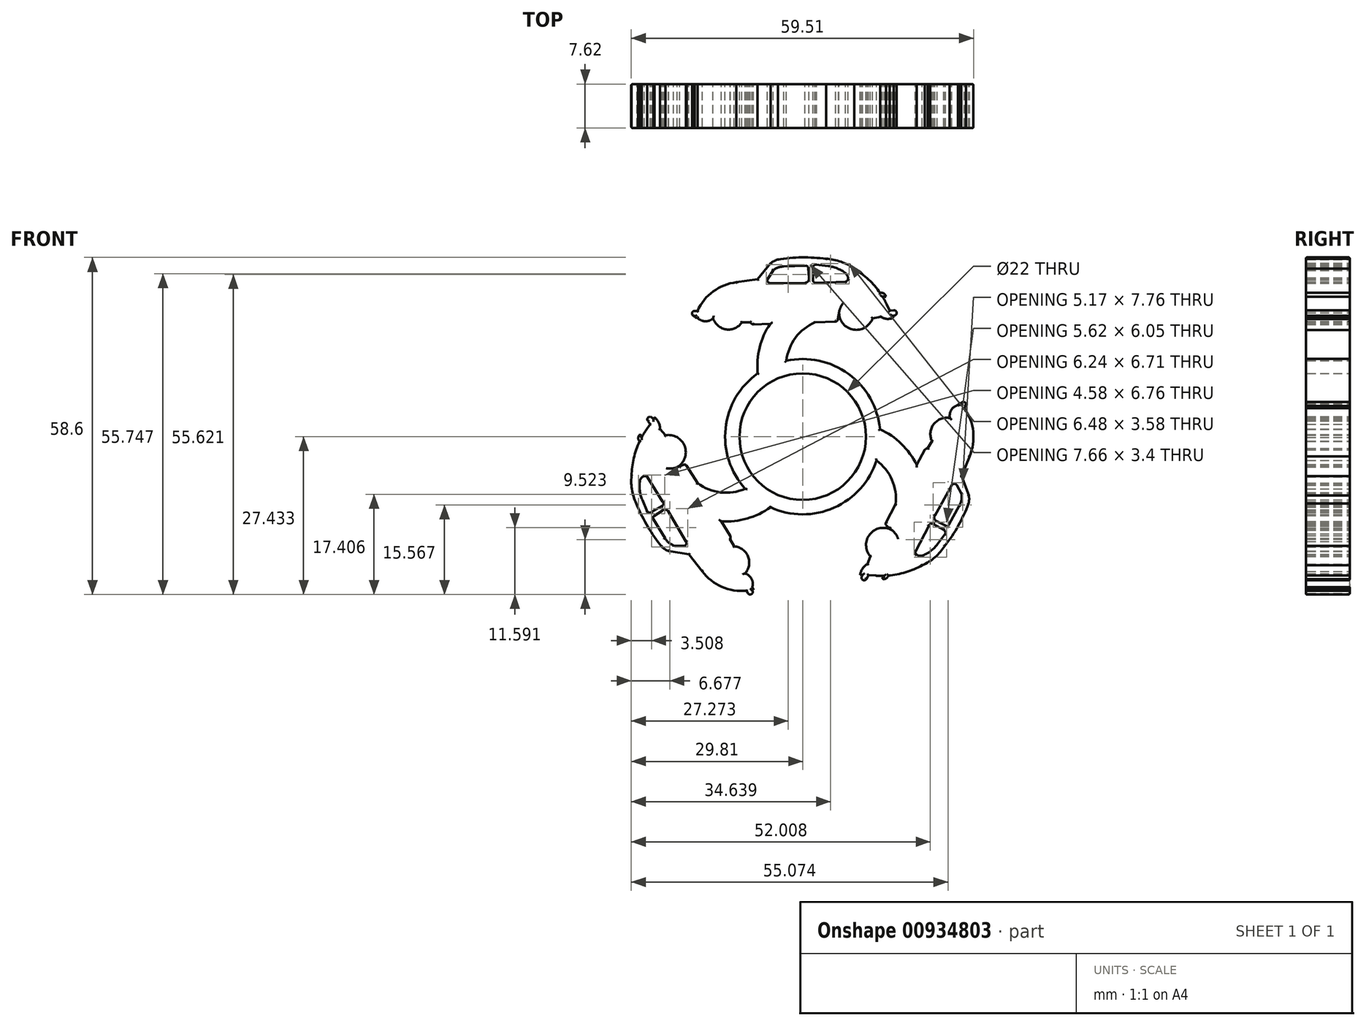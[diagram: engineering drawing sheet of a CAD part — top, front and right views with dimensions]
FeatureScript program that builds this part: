
annotation { "Feature Type Name" : "Feature", "Feature Type Description" : "" }
export const myFeature = defineFeature(function(context is Context, id is Id, definition is map)
    precondition{}
    {
        {
            var Q0;
            Q0=qCreatedBy(makeId("Front.planeOp"),FACE);
            var sketch = newSketch(context, id + "F0", { "sketchPlane" : qUnion([Q0])});
            skArc(sketch, "E0", {"start": v(-11.53, 23.27) * mm, "mid": v(-15.57, 21.68) * mm, "end": v(-18.3, 18.3) * mm});
            skArc(sketch, "E1", {"start": v(8.99, 25.61) * mm, "mid": v(6.65, 26.83) * mm, "end": v(4.07, 27.35) * mm});
            skArc(sketch, "E2", {"start": v(-15.59, 17) * mm, "mid": v(-13.3, 15.08) * mm, "end": v(-10.57, 16.27) * mm});
            skArc(sketch, "E3", {"start": v(6.32, 17.98) * mm, "mid": v(8.82, 15.04) * mm, "end": v(12.15, 17) * mm});
            skPoint(sketch, "E4.first.point", {"position": v(-9.3, 16.64) * mm});
            skPoint(sketch, "E4.second.point", {"position": v(-16.14, 17.08) * mm});
            skPoint(sketch, "E4.third.point", {"position": v(-15.9, 15.72) * mm});
            skPoint(sketch, "E5.first.point", {"position": v(6.84, 18.84) * mm});
            skPoint(sketch, "E5.second.point", {"position": v(12.55, 16.03) * mm});
            skPoint(sketch, "E5.third.point", {"position": v(9.32, 20.48) * mm});
            skLineSegment(sketch, "E6", {"start": v(-7.85, 23.8) * mm, "end": v(-5.6, 26.57) * mm});
            skLineSegment(sketch, "E7", {"start": v(-7.85, 23.8) * mm, "end": v(-11.53, 23.27) * mm});
            skPoint(sketch, "E8.second.point", {"position": v(-0.88, 20.92) * mm});
            skPoint(sketch, "E8.third.point", {"position": v(0.26, 22.68) * mm});
            skPoint(sketch, "E9.first.point", {"position": v(12.94, 17.76) * mm});
            skPoint(sketch, "E9.second.point", {"position": v(14.7, 18.65) * mm});
            skPoint(sketch, "E9.third.point", {"position": v(14.48, 18.97) * mm});
            skPoint(sketch, "E10.first.point", {"position": v(12.5, 18.64) * mm});
            skPoint(sketch, "E10.second.point", {"position": v(16.16, 21.44) * mm});
            skPoint(sketch, "E10.third.point", {"position": v(16.02, 21.52) * mm});
            skPoint(sketch, "E11.first.point", {"position": v(11.44, 23.75) * mm});
            skArc(sketch, "E12", {"start": v(-18.74, 17.14) * mm, "mid": v(-18.5, 17.1) * mm, "end": v(-18.27, 17.1) * mm});
            skPoint(sketch, "E12.first.point", {"position": v(-15.9, 18.25) * mm});
            skPoint(sketch, "E12.second.point", {"position": v(-20.76, 21.48) * mm});
            skPoint(sketch, "E12.third.point", {"position": v(-20.1, 17.77) * mm});
            skArc(sketch, "E13", {"start": v(-9.13, 16.27) * mm, "mid": v(-8.75, 16) * mm, "end": v(-8.27, 15.97) * mm});
            skPoint(sketch, "E13.second.point", {"position": v(-7.64, 17.02) * mm});
            skPoint(sketch, "E13.third.point", {"position": v(-8.6, 15.96) * mm});
            skLineSegment(sketch, "E14.trimOffspring", {"start": v(-8.6, 15.96) * mm, "end": v(-8.27, 15.97) * mm});
            skArc(sketch, "E15.trimOffspring", {"start": v(-4.34, 27.23) * mm, "mid": v(-5, 26.96) * mm, "end": v(-5.6, 26.57) * mm});
            skArc(sketch, "E16.trimOffspring", {"start": v(16.16, 21.44) * mm, "mid": v(16.09, 21.48) * mm, "end": v(16.02, 21.52) * mm});
            skArc(sketch, "E17.trimOffspring", {"start": v(14.61, 19.44) * mm, "mid": v(14.26, 20.12) * mm, "end": v(13.88, 20.77) * mm});
            skPoint(sketch, "E18.first.point", {"position": v(-9.43, 17.2) * mm});
            skPoint(sketch, "E18.second.point", {"position": v(-16.83, 16.34) * mm});
            skPoint(sketch, "E18.third.point", {"position": v(-14.78, 13.44) * mm});
            skArc(sketch, "E19", {"start": v(4.07, 27.35) * mm, "mid": v(-0.14, 27.6) * mm, "end": v(-4.34, 27.23) * mm});
            skPoint(sketch, "E20.end.orphan", {"position": v(4.07, 27.35) * mm});
            skArc(sketch, "E21", {"start": v(14.46, 20.77) * mm, "mid": v(14.1, 21.32) * mm, "end": v(13.47, 21.4) * mm});
            skPoint(sketch, "E21.first.point", {"position": v(13.47, 21.4) * mm});
            skPoint(sketch, "E21.second.point", {"position": v(13.78, 19.9) * mm});
            skPoint(sketch, "E21.third.point", {"position": v(14.26, 20.13) * mm});
            skLineSegment(sketch, "E22", {"start": v(14.46, 20.77) * mm, "end": v(13.88, 20.77) * mm});
            skArc(sketch, "E23.trimOffspring", {"start": v(13.47, 21.4) * mm, "mid": v(11.45, 23.74) * mm, "end": v(8.99, 25.61) * mm});
            skLineSegment(sketch, "E24", {"start": v(14.61, 19.44) * mm, "end": v(15.14, 18.36) * mm});
            skArc(sketch, "E25", {"start": v(15.9, 17.47) * mm, "mid": v(16.34, 17.97) * mm, "end": v(15.83, 18.4) * mm});
            skLineSegment(sketch, "E26", {"start": v(15.9, 17.47) * mm, "end": v(15.59, 17.45) * mm});
            skLineSegment(sketch, "E27", {"start": v(15.83, 18.4) * mm, "end": v(15.14, 18.36) * mm});
            skPoint(sketch, "E27.endSnap0", {"position": v(15.2, 18.26) * mm});
            skPoint(sketch, "E28.orphan", {"position": v(15.2, 18.36) * mm});
            skArc(sketch, "E29", {"start": v(-18.76, 18.3) * mm, "mid": v(-19.25, 17.87) * mm, "end": v(-18.83, 17.37) * mm});
            skArc(sketch, "E30.trimOffspring", {"start": v(-18.67, 17.37) * mm, "mid": v(-18.7, 17.25) * mm, "end": v(-18.74, 17.14) * mm});
            skLineSegment(sketch, "E31", {"start": v(-18.8, 18.3) * mm, "end": v(-18.3, 18.3) * mm});
            skLineSegment(sketch, "E32", {"start": v(-18.83, 17.37) * mm, "end": v(-18.67, 17.37) * mm});
            skPoint(sketch, "E33.orphan", {"position": v(-18.3, 17.38) * mm});
            skPoint(sketch, "E34.orphan", {"position": v(-18.66, 17.38) * mm});
            skLineSegment(sketch, "E35.trimOffspring", {"start": v(15.59, 17.45) * mm, "end": v(15.77, 17.08) * mm});
            skPoint(sketch, "E36.first.point", {"position": v(7.3, 19.61) * mm});
            skPoint(sketch, "E36.second.point", {"position": v(11.9, 14.6) * mm});
            skPoint(sketch, "E36.third.point", {"position": v(12.82, 16.03) * mm});
            skArc(sketch, "E37", {"start": v(5.67, 16.42) * mm, "mid": v(5.96, 16.53) * mm, "end": v(6.12, 16.8) * mm});
            skPoint(sketch, "E37.first.point", {"position": v(6.12, 16.93) * mm});
            skPoint(sketch, "E37.second.point", {"position": v(5.22, 16.82) * mm});
            skPoint(sketch, "E37.third.point", {"position": v(5.67, 16.42) * mm});
            skLineSegment(sketch, "E38", {"start": v(6.23, 17.51) * mm, "end": v(6.12, 16.8) * mm});
            skArc(sketch, "E39.trimOffspring", {"start": v(6.32, 17.98) * mm, "mid": v(6.27, 17.75) * mm, "end": v(6.23, 17.51) * mm});
            skPoint(sketch, "E40.first.point", {"position": v(0.33, 26.04) * mm});
            skPoint(sketch, "E40.second.point", {"position": v(0.73, 25.33) * mm});
            skPoint(sketch, "E40.third.point", {"position": v(0.53, 25.3) * mm});
            skArc(sketch, "E41", {"start": v(0.4, 23.19) * mm, "mid": v(0.94, 23.44) * mm, "end": v(1.07, 24.03) * mm});
            skPoint(sketch, "E41.first.point", {"position": v(1.07, 23.71) * mm});
            skPoint(sketch, "E41.second.point", {"position": v(-0.24, 24.08) * mm});
            skPoint(sketch, "E41.third.point", {"position": v(0.4, 23.19) * mm});
            skArc(sketch, "E42", {"start": v(-6.05, 23.94) * mm, "mid": v(-6.11, 23.4) * mm, "end": v(-5.64, 23.12) * mm});
            skPoint(sketch, "E42.first.point", {"position": v(-5.92, 23.19) * mm});
            skPoint(sketch, "E42.second.point", {"position": v(-5.35, 24) * mm});
            skPoint(sketch, "E42.third.point", {"position": v(-5.6, 24.12) * mm});
            skArc(sketch, "E43", {"start": v(-3.31, 26.01) * mm, "mid": v(-4.29, 25.83) * mm, "end": v(-5.15, 25.33) * mm});
            skPoint(sketch, "E43.first.point", {"position": v(-5.15, 25.33) * mm});
            skPoint(sketch, "E43.second.point", {"position": v(-1.4, 21) * mm});
            skPoint(sketch, "E43.third.point", {"position": v(-0.47, 23.64) * mm});
            skLineSegment(sketch, "E44", {"start": v(-5.15, 25.33) * mm, "end": v(-6.08, 23.9) * mm});
            skLineSegment(sketch, "E45", {"start": v(-3.31, 26.01) * mm, "end": v(0.56, 26.12) * mm});
            skLineSegment(sketch, "E46", {"start": v(-5.64, 23.12) * mm, "end": v(0.4, 23.19) * mm});
            skLineSegment(sketch, "E47", {"start": v(1.07, 24.03) * mm, "end": v(0.98, 25.73) * mm});
            skArc(sketch, "E48.trimOffspring", {"start": v(0.98, 25.73) * mm, "mid": v(0.75, 26.08) * mm, "end": v(0.33, 26.04) * mm});
            skArc(sketch, "E49.trimOffspring", {"start": v(-6.05, 23.95) * mm, "mid": v(-6.05, 23.95) * mm, "end": v(-6.05, 23.94) * mm});
            skArc(sketch, "E50", {"start": v(2.25, 26.33) * mm, "mid": v(1.9, 26.13) * mm, "end": v(1.79, 25.75) * mm});
            skPoint(sketch, "E50.first.point", {"position": v(1.79, 25.85) * mm});
            skPoint(sketch, "E50.second.point", {"position": v(2.85, 25.68) * mm});
            skPoint(sketch, "E50.third.point", {"position": v(2.05, 25.34) * mm});
            skArc(sketch, "E51", {"start": v(1.8, 23.68) * mm, "mid": v(1.96, 23.26) * mm, "end": v(2.41, 23.19) * mm});
            skPoint(sketch, "E51.first.point", {"position": v(1.8, 23.68) * mm});
            skPoint(sketch, "E51.second.point", {"position": v(2.7, 23.57) * mm});
            skPoint(sketch, "E51.third.point", {"position": v(2.7, 23.72) * mm});
            skPoint(sketch, "E52.first.point", {"position": v(7.78, 23.5) * mm});
            skPoint(sketch, "E52.second.point", {"position": v(5.63, 24.43) * mm});
            skPoint(sketch, "E52.third.point", {"position": v(5.78, 23.24) * mm});
            skArc(sketch, "E53", {"start": v(1.79, 25.8) * mm, "mid": v(1.79, 25.8) * mm, "end": v(1.79, 25.8) * mm});
            skPoint(sketch, "E53.first.point", {"position": v(7.41, 24.88) * mm});
            skPoint(sketch, "E53.second.point", {"position": v(-0.05, 15.42) * mm});
            skPoint(sketch, "E53.third.point", {"position": v(3.06, 26.08) * mm});
            skArc(sketch, "E54", {"start": v(7.46, 23.38) * mm, "mid": v(7.7, 23.51) * mm, "end": v(7.85, 23.74) * mm});
            skPoint(sketch, "E54.first.point", {"position": v(7.46, 23.38) * mm});
            skPoint(sketch, "E54.second.point", {"position": v(7.16, 24.47) * mm});
            skPoint(sketch, "E54.third.point", {"position": v(7.12, 24.46) * mm});
            skLineSegment(sketch, "E55", {"start": v(2.41, 23.19) * mm, "end": v(7.46, 23.38) * mm});
            skLineSegment(sketch, "E56", {"start": v(2.25, 26.33) * mm, "end": v(4.45, 26.08) * mm});
            skLineSegment(sketch, "E57", {"start": v(1.79, 25.85) * mm, "end": v(1.8, 23.68) * mm});
            skArc(sketch, "E58.trimOffspring", {"start": v(7.85, 23.74) * mm, "mid": v(7.8, 24.38) * mm, "end": v(7.41, 24.88) * mm});
            skArc(sketch, "E59.trimOffspring", {"start": v(7.41, 24.88) * mm, "mid": v(6, 25.68) * mm, "end": v(4.45, 26.08) * mm});
            skPoint(sketch, "E60.first.point", {"position": v(-17.23, 16.52) * mm});
            skPoint(sketch, "E60.second.point", {"position": v(-16.33, 20.19) * mm});
            skPoint(sketch, "E60.third.point", {"position": v(-16.6, 20.25) * mm});
            skArc(sketch, "E61.trimOffspring", {"start": v(-18.27, 17.1) * mm, "mid": v(-16.95, 16.5) * mm, "end": v(-15.59, 17) * mm});
            skLineSegment(sketch, "E62", {"start": v(-10.57, 16.27) * mm, "end": v(-9.13, 16.27) * mm});
            skLineSegment(sketch, "E63", {"start": v(12.15, 17) * mm, "end": v(13.57, 17.26) * mm});
            skArc(sketch, "E64.trimOffspring", {"start": v(13.57, 17.26) * mm, "mid": v(14.65, 16.9) * mm, "end": v(15.77, 17.08) * mm});
            skPoint(sketch, "E65.1.36", {"position": v(-25.13, -61.05) * mm});
            skPoint(sketch, "E66", {"position": v(-1.45, 16.2) * mm});
            skLineSegment(sketch, "E67", {"start": v(-8.6, 15.96) * mm, "end": v(-5.67, 16.05) * mm});
            skPoint(sketch, "E68", {"position": v(-5.03, 16.07) * mm});
            skPoint(sketch, "E69", {"position": v(2.12, 16.3) * mm});
            skPoint(sketch, "E70.1.0", {"position": v(-12.4, -29.59) * mm});
            skPoint(sketch, "E70.1.1", {"position": v(-24.86, -14.8) * mm});
            skPoint(sketch, "E70.1.2", {"position": v(-14, -20.48) * mm});
            skPoint(sketch, "E70.1.3", {"position": v(-23.25, -2.5) * mm});
            skPoint(sketch, "E70.1.4", {"position": v(-8.43, -31.65) * mm});
            skPoint(sketch, "E70.1.5", {"position": v(-8.75, -26.98) * mm});
            skLineSegment(sketch, "E70.1.6", {"start": v(-24.37, -14.86) * mm, "end": v(-27.06, -10.58) * mm});
            skPoint(sketch, "E70.1.7", {"position": v(-25.81, -18.09) * mm});
            skPoint(sketch, "E70.1.8", {"position": v(-27.2, -3.36) * mm});
            skPoint(sketch, "E70.1.9", {"position": v(-10.94, -28.24) * mm});
            skPoint(sketch, "E70.1.10", {"position": v(-12.85, -21.72) * mm});
            skPoint(sketch, "E70.1.11", {"position": v(-18.27, -11.66) * mm});
            skPoint(sketch, "E70.1.12", {"position": v(-16.41, -13.1) * mm});
            skPoint(sketch, "E70.1.13", {"position": v(-23.32, -17.58) * mm});
            skPoint(sketch, "E70.1.14", {"position": v(-20.15, -8.65) * mm});
            skArc(sketch, "E70.1.15", {"start": v(-28.34, -11.37) * mm, "mid": v(-28.33, -12.99) * mm, "end": v(-27.9, -14.54) * mm});
            skPoint(sketch, "E70.1.16", {"position": v(-28.8, -15.5) * mm});
            skPoint(sketch, "E70.1.17", {"position": v(-20.77, -16.58) * mm});
            skLineSegment(sketch, "E70.1.18", {"start": v(-12.6, -20.78) * mm, "end": v(-14.16, -18.28) * mm});
            skPoint(sketch, "E70.1.19", {"position": v(-26.1, -11.97) * mm});
            skPoint(sketch, "E70.1.20", {"position": v(-21.2, -21.99) * mm});
            skPoint(sketch, "E70.1.21", {"position": v(-21.69, -2.36) * mm});
            skPoint(sketch, "E70.1.22", {"position": v(-7.34, -24.87) * mm});
            skPoint(sketch, "E70.1.23", {"position": v(-25.48, -3.85) * mm});
            skLineSegment(sketch, "E70.1.24", {"start": v(-23.96, -21.22) * mm, "end": v(-26, -17.93) * mm});
            skPoint(sketch, "E70.1.25", {"position": v(-27.33, -10.36) * mm});
            skPoint(sketch, "E70.1.26", {"position": v(-8.81, -30.2) * mm});
            skPoint(sketch, "E70.1.27", {"position": v(-13.28, -22.12) * mm});
            skArc(sketch, "E70.1.28", {"start": v(-28.35, -4.39) * mm, "mid": v(-29.37, -7.3) * mm, "end": v(-29.76, -10.37) * mm});
            skPoint(sketch, "E70.1.29", {"position": v(-26.59, -1.38) * mm});
            skPoint(sketch, "E70.1.30", {"position": v(-12.6, -20.78) * mm});
            skPoint(sketch, "E70.1.31", {"position": v(-25.48, -7.52) * mm});
            skArc(sketch, "E70.1.32", {"start": v(-17.48, -26.97) * mm, "mid": v(-14.08, -29.67) * mm, "end": v(-9.79, -30.36) * mm});
            skPoint(sketch, "E70.1.33", {"position": v(-26.76, -15.72) * mm});
            skArc(sketch, "E70.1.34", {"start": v(-29.76, -10.37) * mm, "mid": v(-29.66, -13) * mm, "end": v(-28.8, -15.5) * mm});
            skPoint(sketch, "E70.1.35", {"position": v(-22.82, -8.85) * mm});
            skArc(sketch, "E70.1.36", {"start": v(-10.03, -27.35) * mm, "mid": v(-9.5, -24.42) * mm, "end": v(-11.9, -22.64) * mm});
            skPoint(sketch, "E70.1.37", {"position": v(-27.06, -10.58) * mm});
            skPoint(sketch, "E70.1.38", {"position": v(-27.65, -3.07) * mm});
            skPoint(sketch, "E70.1.39", {"position": v(-11.31, -34.07) * mm});
            skArc(sketch, "E70.1.40", {"start": v(-21.82, -8.87) * mm, "mid": v(-20.52, -5.23) * mm, "end": v(-23.9, -3.33) * mm});
            skPoint(sketch, "E70.1.41", {"position": v(-9.8, -27.87) * mm});
            skLineSegment(sketch, "E70.1.42", {"start": v(-19.77, -24.04) * mm, "end": v(-23.3, -23.48) * mm});
            skPoint(sketch, "E70.1.43", {"position": v(-27.2, -15.74) * mm});
            skPoint(sketch, "E70.1.44", {"position": v(-28.35, -4.39) * mm});
            skLineSegment(sketch, "E70.1.45", {"start": v(-19.77, -24.04) * mm, "end": v(-17.48, -26.97) * mm});
            skPoint(sketch, "E70.1.46", {"position": v(-23.83, -17.6) * mm});
            skPoint(sketch, "E70.1.47", {"position": v(-22.46, -22.48) * mm});
            skPoint(sketch, "E70.1.48", {"position": v(-20.8, -8.51) * mm});
            skPoint(sketch, "E70.1.49", {"position": v(-29.38, -7.32) * mm});
            skPoint(sketch, "E70.1.50", {"position": v(-22.86, -16.47) * mm});
            skPoint(sketch, "E70.1.51", {"position": v(-16.38, -14.7) * mm});
            skPoint(sketch, "E70.1.52", {"position": v(-21.18, -22.25) * mm});
            skPoint(sketch, "E70.1.53", {"position": v(-23.37, -16.6) * mm});
            skPoint(sketch, "E70.1.54", {"position": v(-9, -29.88) * mm});
            skPoint(sketch, "E70.1.55", {"position": v(-23.38, -2.26) * mm});
            skPoint(sketch, "E70.1.56", {"position": v(-24.94, -3.02) * mm});
            skPoint(sketch, "E70.1.57", {"position": v(-29.74, -2.08) * mm});
            skLineSegment(sketch, "E70.1.58", {"start": v(-20.3, -21.8) * mm, "end": v(-23.37, -16.6) * mm});
            skPoint(sketch, "E70.1.59", {"position": v(-8.78, -28.53) * mm});
            skPoint(sketch, "E70.1.60", {"position": v(-24.5, -15.63) * mm});
            skPoint(sketch, "E70.1.61", {"position": v(-27.06, -12.69) * mm});
            skPoint(sketch, "E70.1.62", {"position": v(-20.21, -22.07) * mm});
            skPoint(sketch, "E70.1.63", {"position": v(-23.72, -8.84) * mm});
            skPoint(sketch, "E70.1.64", {"position": v(-8.83, -28.1) * mm});
            skPoint(sketch, "E70.1.65", {"position": v(-26.76, -2.3) * mm});
            skPoint(sketch, "E70.1.66", {"position": v(-12.32, -29.86) * mm});
            skArc(sketch, "E70.1.67", {"start": v(-28.8, -15.5) * mm, "mid": v(-26.92, -19.27) * mm, "end": v(-24.5, -22.73) * mm});
            skPoint(sketch, "E70.1.68", {"position": v(-24.98, -14.87) * mm});
            skPoint(sketch, "E70.1.69", {"position": v(-14.5, -17.74) * mm});
            skPoint(sketch, "E70.1.70", {"position": v(-28.34, -11.37) * mm});
            skPoint(sketch, "E70.1.71", {"position": v(-20.58, -17.06) * mm});
            skPoint(sketch, "E70.1.72", {"position": v(-20.27, -9.24) * mm});
            skPoint(sketch, "E70.1.73", {"position": v(-26.37, -16.72) * mm});
            skPoint(sketch, "E70.1.74", {"position": v(-25.27, -17.54) * mm});
            skPoint(sketch, "E70.1.75", {"position": v(-29.74, -2.24) * mm});
            skPoint(sketch, "E70.1.76", {"position": v(-26.06, -16.25) * mm});
            skPoint(sketch, "E70.1.77", {"position": v(-26.6, -1.94) * mm});
            skPoint(sketch, "E70.1.78", {"position": v(-27.83, -11.42) * mm});
            skLineSegment(sketch, "E70.1.79", {"start": v(-27.02, -16.57) * mm, "end": v(-27.9, -14.54) * mm});
            skPoint(sketch, "E70.1.80", {"position": v(-25.4, -17.38) * mm});
            skArc(sketch, "E70.1.81", {"start": v(-8.75, -29.72) * mm, "mid": v(-8.9, -28.27) * mm, "end": v(-10.03, -27.35) * mm});
            skArc(sketch, "E70.1.82", {"start": v(-23.96, -21.22) * mm, "mid": v(-23.32, -21.98) * mm, "end": v(-22.46, -22.48) * mm});
            skArc(sketch, "E70.1.83", {"start": v(-21.82, -8.87) * mm, "mid": v(-21.6, -8.8) * mm, "end": v(-21.37, -8.71) * mm});
            skPoint(sketch, "E70.1.84", {"position": v(-26.5, -1.32) * mm});
            skArc(sketch, "E70.1.85", {"start": v(-20.15, -8.65) * mm, "mid": v(-20.39, -8.45) * mm, "end": v(-20.7, -8.46) * mm});
            skPoint(sketch, "E70.1.86", {"position": v(-27.86, -11.39) * mm});
            skArc(sketch, "E70.1.87", {"start": v(-9.56, -30.75) * mm, "mid": v(-8.94, -30.96) * mm, "end": v(-8.72, -30.34) * mm});
            skPoint(sketch, "E70.1.88", {"position": v(-24.16, -16.28) * mm});
            skLineSegment(sketch, "E70.1.89", {"start": v(-23.9, -3.33) * mm, "end": v(-24.82, -2.22) * mm});
            skArc(sketch, "E70.1.90", {"start": v(-28.31, -3.21) * mm, "mid": v(-28.6, -3.79) * mm, "end": v(-28.35, -4.39) * mm});
            skLineSegment(sketch, "E70.1.91", {"start": v(-21.37, -8.71) * mm, "end": v(-20.7, -8.46) * mm});
            skLineSegment(sketch, "E70.1.92", {"start": v(-9.54, -30.8) * mm, "end": v(-9.79, -30.36) * mm});
            skArc(sketch, "E70.1.93", {"start": v(-24.5, -15.63) * mm, "mid": v(-24.21, -15.28) * mm, "end": v(-24.37, -14.86) * mm});
            skArc(sketch, "E70.1.94", {"start": v(-12.62, -21.4) * mm, "mid": v(-12.57, -20.92) * mm, "end": v(-12.78, -20.5) * mm});
            skLineSegment(sketch, "E70.1.95", {"start": v(-11.9, -22.64) * mm, "end": v(-12.62, -21.4) * mm});
            skArc(sketch, "E70.1.96", {"start": v(-25.87, -17.37) * mm, "mid": v(-26.05, -17.74) * mm, "end": v(-25.81, -18.09) * mm});
            skLineSegment(sketch, "E70.1.97", {"start": v(-22.46, -22.48) * mm, "end": v(-20.74, -22.57) * mm});
            skLineSegment(sketch, "E70.1.98", {"start": v(-12.6, -20.78) * mm, "end": v(-12.78, -20.5) * mm});
            skArc(sketch, "E70.1.99", {"start": v(-24.5, -22.73) * mm, "mid": v(-23.94, -23.16) * mm, "end": v(-23.3, -23.48) * mm});
            skArc(sketch, "E70.1.100", {"start": v(-24.82, -2.22) * mm, "mid": v(-25.06, -1.12) * mm, "end": v(-25.76, -0.23) * mm});
            skArc(sketch, "E70.1.101", {"start": v(-29.74, -2.08) * mm, "mid": v(-29.74, -2.16) * mm, "end": v(-29.74, -2.24) * mm});
            skArc(sketch, "E70.1.102", {"start": v(-27.23, -2.42) * mm, "mid": v(-27.64, -3.06) * mm, "end": v(-28.02, -3.72) * mm});
            skLineSegment(sketch, "E70.1.103", {"start": v(-26.37, -16.72) * mm, "end": v(-24.5, -15.63) * mm});
            skLineSegment(sketch, "E70.1.104", {"start": v(-24.43, -16.44) * mm, "end": v(-25.87, -17.37) * mm});
            skLineSegment(sketch, "E70.1.105", {"start": v(-26.17, -0.32) * mm, "end": v(-26, -0.58) * mm});
            skLineSegment(sketch, "E70.1.106", {"start": v(-27.23, -2.42) * mm, "end": v(-26.56, -1.42) * mm});
            skLineSegment(sketch, "E70.1.107", {"start": v(-28.31, -3.21) * mm, "end": v(-28.02, -3.72) * mm});
            skArc(sketch, "E70.1.108", {"start": v(-23.37, -16.6) * mm, "mid": v(-23.86, -16.26) * mm, "end": v(-24.43, -16.44) * mm});
            skArc(sketch, "E70.1.109", {"start": v(-27.58, -10.42) * mm, "mid": v(-28.1, -10.8) * mm, "end": v(-28.34, -11.37) * mm});
            skLineSegment(sketch, "E70.1.110", {"start": v(-26, -0.58) * mm, "end": v(-25.76, -0.23) * mm});
            skArc(sketch, "E70.1.111", {"start": v(-27.06, -10.58) * mm, "mid": v(-27.3, -10.44) * mm, "end": v(-27.58, -10.42) * mm});
            skLineSegment(sketch, "E70.1.112", {"start": v(-26.94, -0.85) * mm, "end": v(-26.56, -1.42) * mm});
            skArc(sketch, "E70.1.113", {"start": v(-26.17, -0.32) * mm, "mid": v(-26.82, -0.2) * mm, "end": v(-26.94, -0.85) * mm});
            skArc(sketch, "E70.1.114", {"start": v(-20.8, -22.56) * mm, "mid": v(-20.3, -22.34) * mm, "end": v(-20.3, -21.8) * mm});
            skArc(sketch, "E70.1.115", {"start": v(-27.02, -16.57) * mm, "mid": v(-26.67, -16.77) * mm, "end": v(-26.28, -16.68) * mm});
            skArc(sketch, "E70.1.116", {"start": v(-26.32, -16.7) * mm, "mid": v(-26.32, -16.7) * mm, "end": v(-26.32, -16.7) * mm});
            skArc(sketch, "E70.1.117", {"start": v(-20.8, -22.56) * mm, "mid": v(-20.8, -22.56) * mm, "end": v(-20.8, -22.56) * mm});
            skLineSegment(sketch, "E70.1.118", {"start": v(-8.72, -30.34) * mm, "end": v(-8.8, -30.2) * mm});
            skArc(sketch, "E70.1.119", {"start": v(-8.8, -30.2) * mm, "mid": v(-8.68, -30.18) * mm, "end": v(-8.56, -30.15) * mm});
            skArc(sketch, "E70.1.120", {"start": v(-8.56, -30.15) * mm, "mid": v(-8.65, -29.93) * mm, "end": v(-8.75, -29.72) * mm});
            skPoint(sketch, "E70.2.0", {"position": v(28.74, -1.3) * mm});
            skPoint(sketch, "E70.2.1", {"position": v(22.15, -19.48) * mm});
            skPoint(sketch, "E70.2.2", {"position": v(21.65, -7.24) * mm});
            skPoint(sketch, "E70.2.3", {"position": v(10.7, -24.24) * mm});
            skPoint(sketch, "E70.2.4", {"position": v(28.54, 3.18) * mm});
            skPoint(sketch, "E70.2.5", {"position": v(24.65, 0.56) * mm});
            skLineSegment(sketch, "E70.2.6", {"start": v(21.96, -19.03) * mm, "end": v(19.6, -23.5) * mm});
            skPoint(sketch, "E70.2.7", {"position": v(25.48, -18.66) * mm});
            skPoint(sketch, "E70.2.8", {"position": v(13.43, -27.23) * mm});
            skPoint(sketch, "E70.2.9", {"position": v(26.84, -0.7) * mm});
            skPoint(sketch, "E70.2.10", {"position": v(22.15, -5.62) * mm});
            skPoint(sketch, "E70.2.11", {"position": v(16.15, -15.34) * mm});
            skPoint(sketch, "E70.2.12", {"position": v(16.47, -13.01) * mm});
            skPoint(sketch, "E70.2.13", {"position": v(23.8, -16.76) * mm});
            skPoint(sketch, "E70.2.14", {"position": v(14.48, -18.47) * mm});
            skArc(sketch, "E70.2.15", {"start": v(20.93, -24.21) * mm, "mid": v(22.33, -23.4) * mm, "end": v(23.45, -22.24) * mm});
            skPoint(sketch, "E70.2.16", {"position": v(24.74, -22.55) * mm});
            skPoint(sketch, "E70.2.17", {"position": v(21.65, -15.05) * mm});
            skLineSegment(sketch, "E70.2.18", {"start": v(21.2, -5.88) * mm, "end": v(19.82, -8.47) * mm});
            skPoint(sketch, "E70.2.19", {"position": v(20.33, -21.97) * mm});
            skPoint(sketch, "E70.2.20", {"position": v(26.55, -12.72) * mm});
            skPoint(sketch, "E70.2.21", {"position": v(9.8, -22.95) * mm});
            skPoint(sketch, "E70.2.22", {"position": v(22.12, 0.73) * mm});
            skPoint(sketch, "E70.2.23", {"position": v(12.98, -25.5) * mm});
            skLineSegment(sketch, "E70.2.24", {"start": v(27.27, -15.49) * mm, "end": v(25.43, -18.9) * mm});
            skPoint(sketch, "E70.2.25", {"position": v(19.55, -23.84) * mm});
            skPoint(sketch, "E70.2.26", {"position": v(27.48, 2.12) * mm});
            skPoint(sketch, "E70.2.27", {"position": v(22.7, -5.79) * mm});
            skArc(sketch, "E70.2.28", {"start": v(14.89, -27.71) * mm, "mid": v(17.93, -27.14) * mm, "end": v(20.78, -25.94) * mm});
            skPoint(sketch, "E70.2.29", {"position": v(11.4, -27.69) * mm});
            skPoint(sketch, "E70.2.30", {"position": v(21.2, -5.88) * mm});
            skPoint(sketch, "E70.2.31", {"position": v(16.17, -23.66) * mm});
            skArc(sketch, "E70.2.32", {"start": v(29, -7) * mm, "mid": v(29.65, -2.7) * mm, "end": v(28.1, 1.35) * mm});
            skPoint(sketch, "E70.2.33", {"position": v(23.9, -20.66) * mm});
            skArc(sketch, "E70.2.34", {"start": v(20.78, -25.94) * mm, "mid": v(23, -24.53) * mm, "end": v(24.74, -22.55) * mm});
            skPoint(sketch, "E70.2.35", {"position": v(15.99, -20.69) * mm});
            skArc(sketch, "E70.2.36", {"start": v(25.61, -0.36) * mm, "mid": v(22.8, -1.37) * mm, "end": v(22.47, -4.33) * mm});
            skPoint(sketch, "E70.2.37", {"position": v(19.6, -23.5) * mm});
            skPoint(sketch, "E70.2.38", {"position": v(13.4, -27.76) * mm});
            skPoint(sketch, "E70.2.39", {"position": v(32.07, 1.89) * mm});
            skArc(sketch, "E70.2.40", {"start": v(15.5, -19.81) * mm, "mid": v(11.7, -20.51) * mm, "end": v(11.74, -24.38) * mm});
            skPoint(sketch, "E70.2.41", {"position": v(25.95, 0.09) * mm});
            skLineSegment(sketch, "E70.2.42", {"start": v(27.62, -10.45) * mm, "end": v(28.9, -13.8) * mm});
            skPoint(sketch, "E70.2.43", {"position": v(24.14, -21.04) * mm});
            skPoint(sketch, "E70.2.44", {"position": v(14.89, -27.71) * mm});
            skLineSegment(sketch, "E70.2.45", {"start": v(27.62, -10.45) * mm, "end": v(29, -7) * mm});
            skPoint(sketch, "E70.2.46", {"position": v(24.07, -17.19) * mm});
            skPoint(sketch, "E70.2.47", {"position": v(27.6, -13.56) * mm});
            skPoint(sketch, "E70.2.48", {"position": v(14.69, -19.11) * mm});
            skPoint(sketch, "E70.2.49", {"position": v(17.94, -27.13) * mm});
            skPoint(sketch, "E70.2.50", {"position": v(22.6, -16.92) * mm});
            skPoint(sketch, "E70.2.51", {"position": v(17.84, -12.19) * mm});
            skPoint(sketch, "E70.2.52", {"position": v(26.77, -12.57) * mm});
            skPoint(sketch, "E70.2.53", {"position": v(22.97, -17.29) * mm});
            skPoint(sketch, "E70.2.54", {"position": v(27.29, 1.8) * mm});
            skPoint(sketch, "E70.2.55", {"position": v(10.56, -24.47) * mm});
            skPoint(sketch, "E70.2.56", {"position": v(12, -25.44) * mm});
            skPoint(sketch, "E70.2.57", {"position": v(13.58, -30.06) * mm});
            skLineSegment(sketch, "E70.2.58", {"start": v(25.93, -12.02) * mm, "end": v(22.97, -17.29) * mm});
            skPoint(sketch, "E70.2.59", {"position": v(26.01, 1.3) * mm});
            skPoint(sketch, "E70.2.60", {"position": v(22.7, -18.75) * mm});
            skPoint(sketch, "E70.2.61", {"position": v(21.43, -22.44) * mm});
            skPoint(sketch, "E70.2.62", {"position": v(26.13, -11.82) * mm});
            skPoint(sketch, "E70.2.63", {"position": v(16.43, -21.47) * mm});
            skPoint(sketch, "E70.2.64", {"position": v(25.65, 1.05) * mm});
            skPoint(sketch, "E70.2.65", {"position": v(12.28, -27.38) * mm});
            skPoint(sketch, "E70.2.66", {"position": v(28.93, -1.1) * mm});
            skArc(sketch, "E70.2.67", {"start": v(24.74, -22.55) * mm, "mid": v(27.06, -19.03) * mm, "end": v(28.84, -15.2) * mm});
            skPoint(sketch, "E70.2.68", {"position": v(22.28, -19.55) * mm});
            skPoint(sketch, "E70.2.69", {"position": v(19.52, -9.03) * mm});
            skPoint(sketch, "E70.2.70", {"position": v(20.93, -24.21) * mm});
            skPoint(sketch, "E70.2.71", {"position": v(21.97, -14.64) * mm});
            skPoint(sketch, "E70.2.72", {"position": v(15.05, -18.28) * mm});
            skPoint(sketch, "E70.2.73", {"position": v(24.58, -19.82) * mm});
            skPoint(sketch, "E70.2.74", {"position": v(24.74, -18.46) * mm});
            skPoint(sketch, "E70.2.75", {"position": v(13.72, -29.99) * mm});
            skPoint(sketch, "E70.2.76", {"position": v(24, -19.8) * mm});
            skPoint(sketch, "E70.2.77", {"position": v(11.89, -27.41) * mm});
            skPoint(sketch, "E70.2.78", {"position": v(20.71, -23.74) * mm});
            skLineSegment(sketch, "E70.2.79", {"start": v(24.77, -20.47) * mm, "end": v(23.45, -22.24) * mm});
            skPoint(sketch, "E70.2.80", {"position": v(24.66, -18.65) * mm});
            skArc(sketch, "E70.2.81", {"start": v(27.03, 1.93) * mm, "mid": v(25.84, 1.08) * mm, "end": v(25.61, -0.36) * mm});
            skArc(sketch, "E70.2.82", {"start": v(27.27, -15.49) * mm, "mid": v(27.6, -14.55) * mm, "end": v(27.6, -13.56) * mm});
            skArc(sketch, "E70.2.83", {"start": v(15.5, -19.81) * mm, "mid": v(15.33, -19.65) * mm, "end": v(15.14, -19.5) * mm});
            skPoint(sketch, "E70.2.84", {"position": v(11.3, -27.63) * mm});
            skArc(sketch, "E70.2.85", {"start": v(14.48, -18.47) * mm, "mid": v(14.42, -18.78) * mm, "end": v(14.59, -19.05) * mm});
            skPoint(sketch, "E70.2.86", {"position": v(20.7, -23.79) * mm});
            skArc(sketch, "E70.2.87", {"start": v(28.32, 1.74) * mm, "mid": v(28.2, 2.39) * mm, "end": v(27.55, 2.27) * mm});
            skPoint(sketch, "E70.2.88", {"position": v(23.09, -18.14) * mm});
            skLineSegment(sketch, "E70.2.89", {"start": v(11.74, -24.38) * mm, "end": v(11.25, -25.73) * mm});
            skArc(sketch, "E70.2.90", {"start": v(13.85, -28.26) * mm, "mid": v(14.5, -28.23) * mm, "end": v(14.89, -27.71) * mm});
            skLineSegment(sketch, "E70.2.91", {"start": v(15.14, -19.5) * mm, "end": v(14.59, -19.05) * mm});
            skLineSegment(sketch, "E70.2.92", {"start": v(28.35, 1.79) * mm, "end": v(28.1, 1.35) * mm});
            skArc(sketch, "E70.2.93", {"start": v(22.7, -18.75) * mm, "mid": v(22.25, -18.68) * mm, "end": v(21.96, -19.03) * mm});
            skArc(sketch, "E70.2.94", {"start": v(21.75, -5.58) * mm, "mid": v(21.31, -5.77) * mm, "end": v(21.05, -6.18) * mm});
            skLineSegment(sketch, "E70.2.95", {"start": v(22.47, -4.33) * mm, "end": v(21.75, -5.58) * mm});
            skArc(sketch, "E70.2.96", {"start": v(24.88, -19.07) * mm, "mid": v(25.3, -19.04) * mm, "end": v(25.48, -18.66) * mm});
            skLineSegment(sketch, "E70.2.97", {"start": v(27.6, -13.56) * mm, "end": v(26.82, -12.03) * mm});
            skLineSegment(sketch, "E70.2.98", {"start": v(21.2, -5.88) * mm, "end": v(21.05, -6.18) * mm});
            skArc(sketch, "E70.2.99", {"start": v(28.84, -15.2) * mm, "mid": v(28.94, -14.5) * mm, "end": v(28.9, -13.8) * mm});
            skArc(sketch, "E70.2.100", {"start": v(11.25, -25.73) * mm, "mid": v(10.4, -26.5) * mm, "end": v(10, -27.54) * mm});
            skArc(sketch, "E70.2.101", {"start": v(13.58, -30.06) * mm, "mid": v(13.65, -30.03) * mm, "end": v(13.72, -29.99) * mm});
            skArc(sketch, "E70.2.102", {"start": v(12.62, -27.72) * mm, "mid": v(13.38, -27.76) * mm, "end": v(14.14, -27.76) * mm});
            skLineSegment(sketch, "E70.2.103", {"start": v(24.58, -19.82) * mm, "end": v(22.7, -18.75) * mm});
            skLineSegment(sketch, "E70.2.104", {"start": v(23.36, -18.3) * mm, "end": v(24.88, -19.07) * mm});
            skLineSegment(sketch, "E70.2.105", {"start": v(10.27, -27.86) * mm, "end": v(10.4, -27.57) * mm});
            skLineSegment(sketch, "E70.2.106", {"start": v(12.62, -27.72) * mm, "end": v(11.42, -27.64) * mm});
            skLineSegment(sketch, "E70.2.107", {"start": v(13.85, -28.26) * mm, "end": v(14.14, -27.76) * mm});
            skArc(sketch, "E70.2.108", {"start": v(22.97, -17.29) * mm, "mid": v(22.92, -17.89) * mm, "end": v(23.36, -18.3) * mm});
            skArc(sketch, "E70.2.109", {"start": v(19.73, -24.02) * mm, "mid": v(20.3, -24.29) * mm, "end": v(20.93, -24.21) * mm});
            skLineSegment(sketch, "E70.2.110", {"start": v(10.4, -27.57) * mm, "end": v(10, -27.54) * mm});
            skArc(sketch, "E70.2.111", {"start": v(19.6, -23.5) * mm, "mid": v(19.6, -23.77) * mm, "end": v(19.73, -24.02) * mm});
            skLineSegment(sketch, "E70.2.112", {"start": v(11.11, -28.26) * mm, "end": v(11.42, -27.64) * mm});
            skArc(sketch, "E70.2.113", {"start": v(10.27, -27.86) * mm, "mid": v(10.49, -28.48) * mm, "end": v(11.11, -28.26) * mm});
            skArc(sketch, "E70.2.114", {"start": v(26.85, -12.08) * mm, "mid": v(26.4, -11.76) * mm, "end": v(25.93, -12.02) * mm});
            skArc(sketch, "E70.2.115", {"start": v(24.77, -20.47) * mm, "mid": v(24.77, -20.07) * mm, "end": v(24.5, -19.77) * mm});
            skArc(sketch, "E70.2.116", {"start": v(24.53, -19.8) * mm, "mid": v(24.53, -19.8) * mm, "end": v(24.53, -19.8) * mm});
            skArc(sketch, "E70.2.117", {"start": v(26.86, -12.1) * mm, "mid": v(26.85, -12.09) * mm, "end": v(26.85, -12.08) * mm});
            skLineSegment(sketch, "E70.2.118", {"start": v(27.55, 2.27) * mm, "end": v(27.47, 2.13) * mm});
            skArc(sketch, "E70.2.119", {"start": v(27.47, 2.13) * mm, "mid": v(27.38, 2.22) * mm, "end": v(27.3, 2.31) * mm});
            skArc(sketch, "E70.2.120", {"start": v(27.3, 2.31) * mm, "mid": v(27.15, 2.12) * mm, "end": v(27.03, 1.93) * mm});
            skPoint(sketch, "E70.center", {"position": v(0, -3.57) * mm});
            skCircle(sketch, "E71", {"center": v(0, -3.57) * mm, "radius": 11 * mm});
            skArc(sketch, "E72", {"start": v(-7.84, 7.43) * mm, "mid": v(-13.42, -2.11) * mm, "end": v(-10, -12.63) * mm});
            skPoint(sketch, "E73.second.point", {"position": v(8.65, 1.04) * mm});
            skPoint(sketch, "E73.third.point", {"position": v(3.4, 0.63) * mm});
            skArc(sketch, "E74.0", {"start": v(-5.67, 16.05) * mm, "mid": v(-7.5, 11.93) * mm, "end": v(-7.84, 7.43) * mm});
            skArc(sketch, "E75.trimOffspring", {"start": v(2.12, 16.3) * mm, "mid": v(-1.26, 13.64) * mm, "end": v(-2.84, 9.63) * mm});
            skLineSegment(sketch, "E76.trimOffspring", {"start": v(2.12, 16.3) * mm, "end": v(5.7, 16.43) * mm});
            skArc(sketch, "E77.1.0", {"start": v(-18.27, -11.66) * mm, "mid": v(-14.27, -13.26) * mm, "end": v(-10, -12.63) * mm});
            skArc(sketch, "E77.1.1", {"start": v(-14.16, -18.28) * mm, "mid": v(-9.67, -17.8) * mm, "end": v(-5.6, -15.85) * mm});
            skArc(sketch, "E77.2.0", {"start": v(16.15, -15.34) * mm, "mid": v(15.53, -11.08) * mm, "end": v(12.85, -7.7) * mm});
            skArc(sketch, "E77.2.1", {"start": v(19.82, -8.47) * mm, "mid": v(17.16, -4.82) * mm, "end": v(13.44, -2.28) * mm});
            skArc(sketch, "E78.trimOffspring", {"start": v(-5.6, -15.85) * mm, "mid": v(5.45, -15.92) * mm, "end": v(12.85, -7.7) * mm});
            skArc(sketch, "E79.trimOffspring", {"start": v(13.44, -2.28) * mm, "mid": v(7.97, 7.33) * mm, "end": v(-2.84, 9.63) * mm});
            skLineSegment(sketch, "E80.trimOffspring", {"start": v(-18.27, -11.66) * mm, "end": v(-20.16, -8.63) * mm});
            skLineSegment(sketch, "E81.trimOffspring", {"start": v(16.15, -15.34) * mm, "end": v(14.46, -18.5) * mm});
            skSolve(sketch);
        }
        {
            var Q0;
            {var subQ37=sQuery(id+"F0.wireOp",EDGE,"E0");Q0=makeQuery(id+"F0.imprint","IMPRINT",FACE,{"disambiguationData":[TD([[makeQuery(id+"F0.imprint","IMPRINT",EDGE,{"derivedFrom":subQ37}),1.0]])]});}
            extrude(context, id + "F1", {"entities" : qUnion([Q0]), "depth" : 7.62 * mm, "offsetDistance" : 25 * mm});
        }
        {
            var Q0;
            Q0=makeQuery(id+"F1.opExtrude","CAP_FACE",FACE,{"disambiguationData":[OSD([sQuery(id+"F0.wireOp",EDGE,"E0"),sQuery(id+"F0.wireOp",EDGE,"E1"),sQuery(id+"F0.wireOp",EDGE,"E2"),sQuery(id+"F0.wireOp",EDGE,"E3"),sQuery(id+"F0.wireOp",EDGE,"E6"),sQuery(id+"F0.wireOp",EDGE,"E7"),sQuery(id+"F0.wireOp",EDGE,"E12"),sQuery(id+"F0.wireOp",EDGE,"E13"),sQuery(id+"F0.wireOp",EDGE,"E15.trimOffspring"),sQuery(id+"F0.wireOp",EDGE,"E17.trimOffspring"),sQuery(id+"F0.wireOp",EDGE,"E19"),sQuery(id+"F0.wireOp",EDGE,"E21"),sQuery(id+"F0.wireOp",EDGE,"E22"),sQuery(id+"F0.wireOp",EDGE,"E23.trimOffspring"),sQuery(id+"F0.wireOp",EDGE,"E24"),sQuery(id+"F0.wireOp",EDGE,"E25"),sQuery(id+"F0.wireOp",EDGE,"E26"),sQuery(id+"F0.wireOp",EDGE,"E27"),sQuery(id+"F0.wireOp",EDGE,"E29"),sQuery(id+"F0.wireOp",EDGE,"E30.trimOffspring"),sQuery(id+"F0.wireOp",EDGE,"E31"),sQuery(id+"F0.wireOp",EDGE,"E32"),sQuery(id+"F0.wireOp",EDGE,"E35.trimOffspring"),sQuery(id+"F0.wireOp",EDGE,"E37"),sQuery(id+"F0.wireOp",EDGE,"E38"),sQuery(id+"F0.wireOp",EDGE,"E39.trimOffspring"),sQuery(id+"F0.wireOp",EDGE,"E41"),sQuery(id+"F0.wireOp",EDGE,"E42"),sQuery(id+"F0.wireOp",EDGE,"E43"),sQuery(id+"F0.wireOp",EDGE,"E44"),sQuery(id+"F0.wireOp",EDGE,"E45"),sQuery(id+"F0.wireOp",EDGE,"E46"),sQuery(id+"F0.wireOp",EDGE,"E47"),sQuery(id+"F0.wireOp",EDGE,"E48.trimOffspring"),sQuery(id+"F0.wireOp",EDGE,"E50"),sQuery(id+"F0.wireOp",EDGE,"E51"),sQuery(id+"F0.wireOp",EDGE,"E54"),sQuery(id+"F0.wireOp",EDGE,"E55"),sQuery(id+"F0.wireOp",EDGE,"E56"),sQuery(id+"F0.wireOp",EDGE,"E57"),sQuery(id+"F0.wireOp",EDGE,"E58.trimOffspring"),sQuery(id+"F0.wireOp",EDGE,"E59.trimOffspring"),sQuery(id+"F0.wireOp",EDGE,"E61.trimOffspring"),sQuery(id+"F0.wireOp",EDGE,"E62"),sQuery(id+"F0.wireOp",EDGE,"E63"),sQuery(id+"F0.wireOp",EDGE,"E64.trimOffspring"),sQuery(id+"F0.wireOp",EDGE,"E67"),sQuery(id+"F0.wireOp",EDGE,"E70.1.6"),sQuery(id+"F0.wireOp",EDGE,"E70.1.15"),sQuery(id+"F0.wireOp",EDGE,"E70.1.18"),sQuery(id+"F0.wireOp",EDGE,"E70.1.24"),sQuery(id+"F0.wireOp",EDGE,"E70.1.28"),sQuery(id+"F0.wireOp",EDGE,"E70.1.32"),sQuery(id+"F0.wireOp",EDGE,"E70.1.34"),sQuery(id+"F0.wireOp",EDGE,"E70.1.36"),sQuery(id+"F0.wireOp",EDGE,"E70.1.40"),sQuery(id+"F0.wireOp",EDGE,"E70.1.42"),sQuery(id+"F0.wireOp",EDGE,"E70.1.45"),sQuery(id+"F0.wireOp",EDGE,"E70.1.58"),sQuery(id+"F0.wireOp",EDGE,"E70.1.67"),sQuery(id+"F0.wireOp",EDGE,"E70.1.79"),sQuery(id+"F0.wireOp",EDGE,"E70.1.81"),sQuery(id+"F0.wireOp",EDGE,"E70.1.82"),sQuery(id+"F0.wireOp",EDGE,"E70.1.83"),sQuery(id+"F0.wireOp",EDGE,"E70.1.85"),sQuery(id+"F0.wireOp",EDGE,"E70.1.87"),sQuery(id+"F0.wireOp",EDGE,"E70.1.89"),sQuery(id+"F0.wireOp",EDGE,"E70.1.90"),sQuery(id+"F0.wireOp",EDGE,"E70.1.91"),sQuery(id+"F0.wireOp",EDGE,"E70.1.92"),sQuery(id+"F0.wireOp",EDGE,"E70.1.93"),sQuery(id+"F0.wireOp",EDGE,"E70.1.94"),sQuery(id+"F0.wireOp",EDGE,"E70.1.95"),sQuery(id+"F0.wireOp",EDGE,"E70.1.96"),sQuery(id+"F0.wireOp",EDGE,"E70.1.97"),sQuery(id+"F0.wireOp",EDGE,"E70.1.98"),sQuery(id+"F0.wireOp",EDGE,"E70.1.99"),sQuery(id+"F0.wireOp",EDGE,"E70.1.100"),sQuery(id+"F0.wireOp",EDGE,"E70.1.102"),sQuery(id+"F0.wireOp",EDGE,"E70.1.103"),sQuery(id+"F0.wireOp",EDGE,"E70.1.104"),sQuery(id+"F0.wireOp",EDGE,"E70.1.105"),sQuery(id+"F0.wireOp",EDGE,"E70.1.106"),sQuery(id+"F0.wireOp",EDGE,"E70.1.107"),sQuery(id+"F0.wireOp",EDGE,"E70.1.108"),sQuery(id+"F0.wireOp",EDGE,"E70.1.109"),sQuery(id+"F0.wireOp",EDGE,"E70.1.110"),sQuery(id+"F0.wireOp",EDGE,"E70.1.111"),sQuery(id+"F0.wireOp",EDGE,"E70.1.112"),sQuery(id+"F0.wireOp",EDGE,"E70.1.113"),sQuery(id+"F0.wireOp",EDGE,"E70.1.114"),sQuery(id+"F0.wireOp",EDGE,"E70.1.115"),sQuery(id+"F0.wireOp",EDGE,"E70.1.118"),sQuery(id+"F0.wireOp",EDGE,"E70.1.119"),sQuery(id+"F0.wireOp",EDGE,"E70.1.120"),sQuery(id+"F0.wireOp",EDGE,"E70.2.6"),sQuery(id+"F0.wireOp",EDGE,"E70.2.15"),sQuery(id+"F0.wireOp",EDGE,"E70.2.18"),sQuery(id+"F0.wireOp",EDGE,"E70.2.24"),sQuery(id+"F0.wireOp",EDGE,"E70.2.28"),sQuery(id+"F0.wireOp",EDGE,"E70.2.32"),sQuery(id+"F0.wireOp",EDGE,"E70.2.34"),sQuery(id+"F0.wireOp",EDGE,"E70.2.36"),sQuery(id+"F0.wireOp",EDGE,"E70.2.40"),sQuery(id+"F0.wireOp",EDGE,"E70.2.42"),sQuery(id+"F0.wireOp",EDGE,"E70.2.45"),sQuery(id+"F0.wireOp",EDGE,"E70.2.58"),sQuery(id+"F0.wireOp",EDGE,"E70.2.67"),sQuery(id+"F0.wireOp",EDGE,"E70.2.79"),sQuery(id+"F0.wireOp",EDGE,"E70.2.81"),sQuery(id+"F0.wireOp",EDGE,"E70.2.82"),sQuery(id+"F0.wireOp",EDGE,"E70.2.83"),sQuery(id+"F0.wireOp",EDGE,"E70.2.85"),sQuery(id+"F0.wireOp",EDGE,"E70.2.87"),sQuery(id+"F0.wireOp",EDGE,"E70.2.89"),sQuery(id+"F0.wireOp",EDGE,"E70.2.90"),sQuery(id+"F0.wireOp",EDGE,"E70.2.91"),sQuery(id+"F0.wireOp",EDGE,"E70.2.92"),sQuery(id+"F0.wireOp",EDGE,"E70.2.93"),sQuery(id+"F0.wireOp",EDGE,"E70.2.94"),sQuery(id+"F0.wireOp",EDGE,"E70.2.95"),sQuery(id+"F0.wireOp",EDGE,"E70.2.96"),sQuery(id+"F0.wireOp",EDGE,"E70.2.97"),sQuery(id+"F0.wireOp",EDGE,"E70.2.98"),sQuery(id+"F0.wireOp",EDGE,"E70.2.99"),sQuery(id+"F0.wireOp",EDGE,"E70.2.100"),sQuery(id+"F0.wireOp",EDGE,"E70.2.102"),sQuery(id+"F0.wireOp",EDGE,"E70.2.103"),sQuery(id+"F0.wireOp",EDGE,"E70.2.104"),sQuery(id+"F0.wireOp",EDGE,"E70.2.105"),sQuery(id+"F0.wireOp",EDGE,"E70.2.106"),sQuery(id+"F0.wireOp",EDGE,"E70.2.107"),sQuery(id+"F0.wireOp",EDGE,"E70.2.108"),sQuery(id+"F0.wireOp",EDGE,"E70.2.109"),sQuery(id+"F0.wireOp",EDGE,"E70.2.110"),sQuery(id+"F0.wireOp",EDGE,"E70.2.111"),sQuery(id+"F0.wireOp",EDGE,"E70.2.112"),sQuery(id+"F0.wireOp",EDGE,"E70.2.113"),sQuery(id+"F0.wireOp",EDGE,"E70.2.114"),sQuery(id+"F0.wireOp",EDGE,"E70.2.115"),sQuery(id+"F0.wireOp",EDGE,"E70.2.118"),sQuery(id+"F0.wireOp",EDGE,"E70.2.119"),sQuery(id+"F0.wireOp",EDGE,"E70.2.120"),sQuery(id+"F0.wireOp",EDGE,"E71"),sQuery(id+"F0.wireOp",EDGE,"E72"),sQuery(id+"F0.wireOp",EDGE,"E74.0"),sQuery(id+"F0.wireOp",EDGE,"E75.trimOffspring"),sQuery(id+"F0.wireOp",EDGE,"E76.trimOffspring"),sQuery(id+"F0.wireOp",EDGE,"E77.1.0"),sQuery(id+"F0.wireOp",EDGE,"E77.1.1"),sQuery(id+"F0.wireOp",EDGE,"E77.2.0"),sQuery(id+"F0.wireOp",EDGE,"E77.2.1"),sQuery(id+"F0.wireOp",EDGE,"E78.trimOffspring"),sQuery(id+"F0.wireOp",EDGE,"E79.trimOffspring"),sQuery(id+"F0.wireOp",EDGE,"E80.trimOffspring"),sQuery(id+"F0.wireOp",EDGE,"E81.trimOffspring")])],"isStart":false});
            var Q1;
            Q1=makeQuery(id+"F1.opExtrude","CAP_FACE",FACE,{"disambiguationData":[OSD([sQuery(id+"F0.wireOp",EDGE,"E0"),sQuery(id+"F0.wireOp",EDGE,"E1"),sQuery(id+"F0.wireOp",EDGE,"E2"),sQuery(id+"F0.wireOp",EDGE,"E3"),sQuery(id+"F0.wireOp",EDGE,"E6"),sQuery(id+"F0.wireOp",EDGE,"E7"),sQuery(id+"F0.wireOp",EDGE,"E12"),sQuery(id+"F0.wireOp",EDGE,"E13"),sQuery(id+"F0.wireOp",EDGE,"E15.trimOffspring"),sQuery(id+"F0.wireOp",EDGE,"E17.trimOffspring"),sQuery(id+"F0.wireOp",EDGE,"E19"),sQuery(id+"F0.wireOp",EDGE,"E21"),sQuery(id+"F0.wireOp",EDGE,"E22"),sQuery(id+"F0.wireOp",EDGE,"E23.trimOffspring"),sQuery(id+"F0.wireOp",EDGE,"E24"),sQuery(id+"F0.wireOp",EDGE,"E25"),sQuery(id+"F0.wireOp",EDGE,"E26"),sQuery(id+"F0.wireOp",EDGE,"E27"),sQuery(id+"F0.wireOp",EDGE,"E29"),sQuery(id+"F0.wireOp",EDGE,"E30.trimOffspring"),sQuery(id+"F0.wireOp",EDGE,"E31"),sQuery(id+"F0.wireOp",EDGE,"E32"),sQuery(id+"F0.wireOp",EDGE,"E35.trimOffspring"),sQuery(id+"F0.wireOp",EDGE,"E37"),sQuery(id+"F0.wireOp",EDGE,"E38"),sQuery(id+"F0.wireOp",EDGE,"E39.trimOffspring"),sQuery(id+"F0.wireOp",EDGE,"E41"),sQuery(id+"F0.wireOp",EDGE,"E42"),sQuery(id+"F0.wireOp",EDGE,"E43"),sQuery(id+"F0.wireOp",EDGE,"E44"),sQuery(id+"F0.wireOp",EDGE,"E45"),sQuery(id+"F0.wireOp",EDGE,"E46"),sQuery(id+"F0.wireOp",EDGE,"E47"),sQuery(id+"F0.wireOp",EDGE,"E48.trimOffspring"),sQuery(id+"F0.wireOp",EDGE,"E50"),sQuery(id+"F0.wireOp",EDGE,"E51"),sQuery(id+"F0.wireOp",EDGE,"E54"),sQuery(id+"F0.wireOp",EDGE,"E55"),sQuery(id+"F0.wireOp",EDGE,"E56"),sQuery(id+"F0.wireOp",EDGE,"E57"),sQuery(id+"F0.wireOp",EDGE,"E58.trimOffspring"),sQuery(id+"F0.wireOp",EDGE,"E59.trimOffspring"),sQuery(id+"F0.wireOp",EDGE,"E61.trimOffspring"),sQuery(id+"F0.wireOp",EDGE,"E62"),sQuery(id+"F0.wireOp",EDGE,"E63"),sQuery(id+"F0.wireOp",EDGE,"E64.trimOffspring"),sQuery(id+"F0.wireOp",EDGE,"E67"),sQuery(id+"F0.wireOp",EDGE,"E70.1.6"),sQuery(id+"F0.wireOp",EDGE,"E70.1.15"),sQuery(id+"F0.wireOp",EDGE,"E70.1.18"),sQuery(id+"F0.wireOp",EDGE,"E70.1.24"),sQuery(id+"F0.wireOp",EDGE,"E70.1.28"),sQuery(id+"F0.wireOp",EDGE,"E70.1.32"),sQuery(id+"F0.wireOp",EDGE,"E70.1.34"),sQuery(id+"F0.wireOp",EDGE,"E70.1.36"),sQuery(id+"F0.wireOp",EDGE,"E70.1.40"),sQuery(id+"F0.wireOp",EDGE,"E70.1.42"),sQuery(id+"F0.wireOp",EDGE,"E70.1.45"),sQuery(id+"F0.wireOp",EDGE,"E70.1.58"),sQuery(id+"F0.wireOp",EDGE,"E70.1.67"),sQuery(id+"F0.wireOp",EDGE,"E70.1.79"),sQuery(id+"F0.wireOp",EDGE,"E70.1.81"),sQuery(id+"F0.wireOp",EDGE,"E70.1.82"),sQuery(id+"F0.wireOp",EDGE,"E70.1.83"),sQuery(id+"F0.wireOp",EDGE,"E70.1.85"),sQuery(id+"F0.wireOp",EDGE,"E70.1.87"),sQuery(id+"F0.wireOp",EDGE,"E70.1.89"),sQuery(id+"F0.wireOp",EDGE,"E70.1.90"),sQuery(id+"F0.wireOp",EDGE,"E70.1.91"),sQuery(id+"F0.wireOp",EDGE,"E70.1.92"),sQuery(id+"F0.wireOp",EDGE,"E70.1.93"),sQuery(id+"F0.wireOp",EDGE,"E70.1.94"),sQuery(id+"F0.wireOp",EDGE,"E70.1.95"),sQuery(id+"F0.wireOp",EDGE,"E70.1.96"),sQuery(id+"F0.wireOp",EDGE,"E70.1.97"),sQuery(id+"F0.wireOp",EDGE,"E70.1.98"),sQuery(id+"F0.wireOp",EDGE,"E70.1.99"),sQuery(id+"F0.wireOp",EDGE,"E70.1.100"),sQuery(id+"F0.wireOp",EDGE,"E70.1.102"),sQuery(id+"F0.wireOp",EDGE,"E70.1.103"),sQuery(id+"F0.wireOp",EDGE,"E70.1.104"),sQuery(id+"F0.wireOp",EDGE,"E70.1.105"),sQuery(id+"F0.wireOp",EDGE,"E70.1.106"),sQuery(id+"F0.wireOp",EDGE,"E70.1.107"),sQuery(id+"F0.wireOp",EDGE,"E70.1.108"),sQuery(id+"F0.wireOp",EDGE,"E70.1.109"),sQuery(id+"F0.wireOp",EDGE,"E70.1.110"),sQuery(id+"F0.wireOp",EDGE,"E70.1.111"),sQuery(id+"F0.wireOp",EDGE,"E70.1.112"),sQuery(id+"F0.wireOp",EDGE,"E70.1.113"),sQuery(id+"F0.wireOp",EDGE,"E70.1.114"),sQuery(id+"F0.wireOp",EDGE,"E70.1.115"),sQuery(id+"F0.wireOp",EDGE,"E70.1.118"),sQuery(id+"F0.wireOp",EDGE,"E70.1.119"),sQuery(id+"F0.wireOp",EDGE,"E70.1.120"),sQuery(id+"F0.wireOp",EDGE,"E70.2.6"),sQuery(id+"F0.wireOp",EDGE,"E70.2.15"),sQuery(id+"F0.wireOp",EDGE,"E70.2.18"),sQuery(id+"F0.wireOp",EDGE,"E70.2.24"),sQuery(id+"F0.wireOp",EDGE,"E70.2.28"),sQuery(id+"F0.wireOp",EDGE,"E70.2.32"),sQuery(id+"F0.wireOp",EDGE,"E70.2.34"),sQuery(id+"F0.wireOp",EDGE,"E70.2.36"),sQuery(id+"F0.wireOp",EDGE,"E70.2.40"),sQuery(id+"F0.wireOp",EDGE,"E70.2.42"),sQuery(id+"F0.wireOp",EDGE,"E70.2.45"),sQuery(id+"F0.wireOp",EDGE,"E70.2.58"),sQuery(id+"F0.wireOp",EDGE,"E70.2.67"),sQuery(id+"F0.wireOp",EDGE,"E70.2.79"),sQuery(id+"F0.wireOp",EDGE,"E70.2.81"),sQuery(id+"F0.wireOp",EDGE,"E70.2.82"),sQuery(id+"F0.wireOp",EDGE,"E70.2.83"),sQuery(id+"F0.wireOp",EDGE,"E70.2.85"),sQuery(id+"F0.wireOp",EDGE,"E70.2.87"),sQuery(id+"F0.wireOp",EDGE,"E70.2.89"),sQuery(id+"F0.wireOp",EDGE,"E70.2.90"),sQuery(id+"F0.wireOp",EDGE,"E70.2.91"),sQuery(id+"F0.wireOp",EDGE,"E70.2.92"),sQuery(id+"F0.wireOp",EDGE,"E70.2.93"),sQuery(id+"F0.wireOp",EDGE,"E70.2.94"),sQuery(id+"F0.wireOp",EDGE,"E70.2.95"),sQuery(id+"F0.wireOp",EDGE,"E70.2.96"),sQuery(id+"F0.wireOp",EDGE,"E70.2.97"),sQuery(id+"F0.wireOp",EDGE,"E70.2.98"),sQuery(id+"F0.wireOp",EDGE,"E70.2.99"),sQuery(id+"F0.wireOp",EDGE,"E70.2.100"),sQuery(id+"F0.wireOp",EDGE,"E70.2.102"),sQuery(id+"F0.wireOp",EDGE,"E70.2.103"),sQuery(id+"F0.wireOp",EDGE,"E70.2.104"),sQuery(id+"F0.wireOp",EDGE,"E70.2.105"),sQuery(id+"F0.wireOp",EDGE,"E70.2.106"),sQuery(id+"F0.wireOp",EDGE,"E70.2.107"),sQuery(id+"F0.wireOp",EDGE,"E70.2.108"),sQuery(id+"F0.wireOp",EDGE,"E70.2.109"),sQuery(id+"F0.wireOp",EDGE,"E70.2.110"),sQuery(id+"F0.wireOp",EDGE,"E70.2.111"),sQuery(id+"F0.wireOp",EDGE,"E70.2.112"),sQuery(id+"F0.wireOp",EDGE,"E70.2.113"),sQuery(id+"F0.wireOp",EDGE,"E70.2.114"),sQuery(id+"F0.wireOp",EDGE,"E70.2.115"),sQuery(id+"F0.wireOp",EDGE,"E70.2.118"),sQuery(id+"F0.wireOp",EDGE,"E70.2.119"),sQuery(id+"F0.wireOp",EDGE,"E70.2.120"),sQuery(id+"F0.wireOp",EDGE,"E71"),sQuery(id+"F0.wireOp",EDGE,"E72"),sQuery(id+"F0.wireOp",EDGE,"E74.0"),sQuery(id+"F0.wireOp",EDGE,"E75.trimOffspring"),sQuery(id+"F0.wireOp",EDGE,"E76.trimOffspring"),sQuery(id+"F0.wireOp",EDGE,"E77.1.0"),sQuery(id+"F0.wireOp",EDGE,"E77.1.1"),sQuery(id+"F0.wireOp",EDGE,"E77.2.0"),sQuery(id+"F0.wireOp",EDGE,"E77.2.1"),sQuery(id+"F0.wireOp",EDGE,"E78.trimOffspring"),sQuery(id+"F0.wireOp",EDGE,"E79.trimOffspring"),sQuery(id+"F0.wireOp",EDGE,"E80.trimOffspring"),sQuery(id+"F0.wireOp",EDGE,"E81.trimOffspring")])],"isStart":true});
            fillet(context, id + "F2", {"entities" : qUnion([Q0, Q1]), "radius" : .2 * mm, "tangentPropagation" : true, "allowEdgeOverflow" : false});
        }
    });
